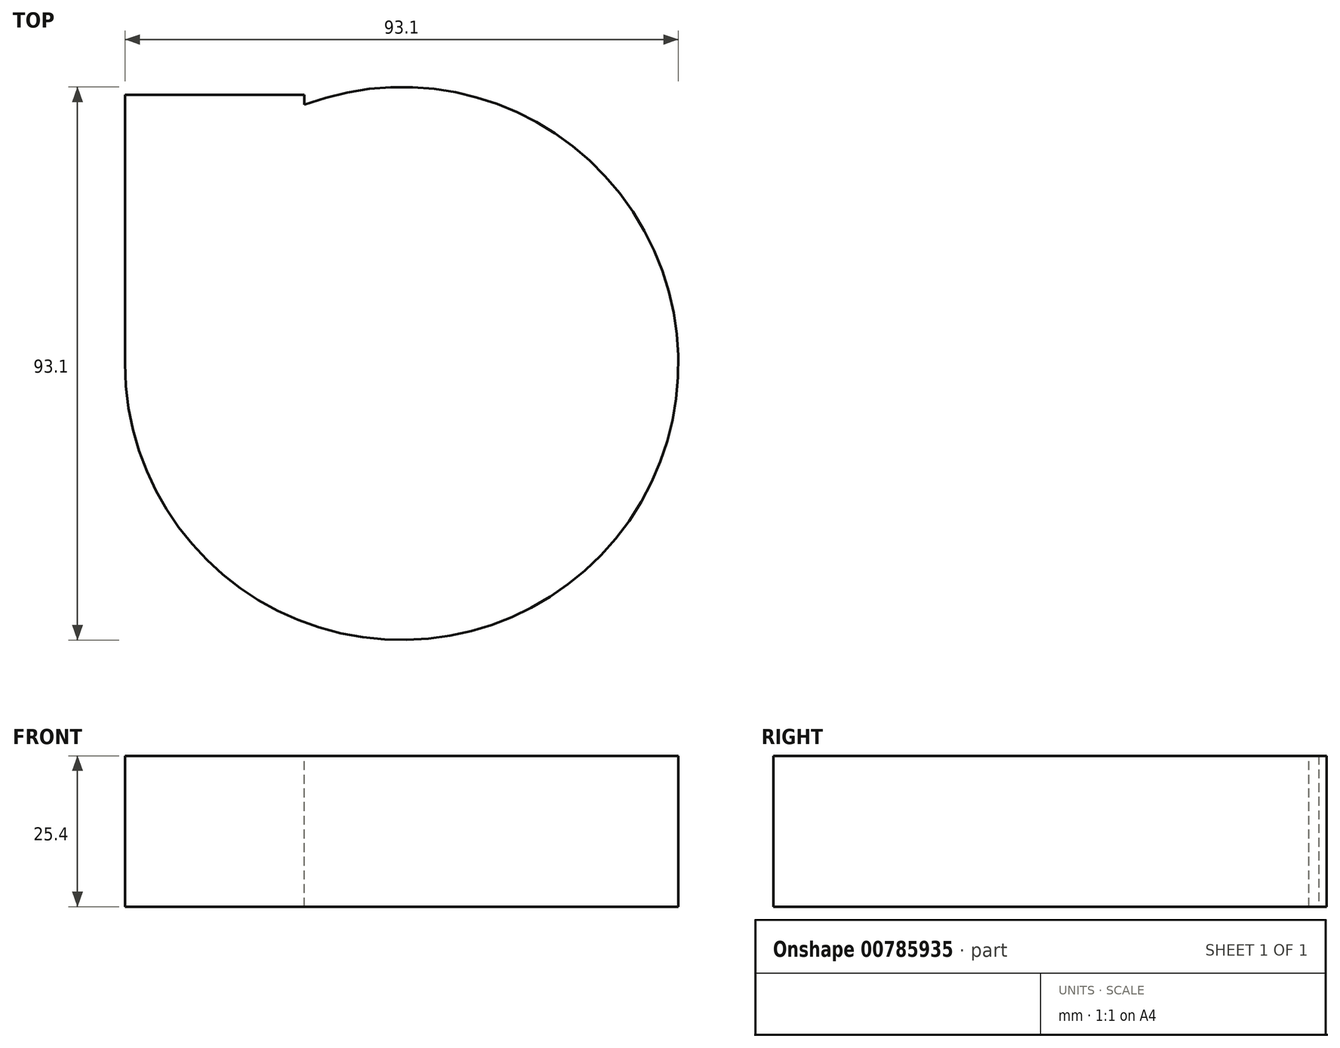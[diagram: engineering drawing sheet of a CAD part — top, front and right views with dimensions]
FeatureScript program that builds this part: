
annotation { "Feature Type Name" : "Feature", "Feature Type Description" : "" }
export const myFeature = defineFeature(function(context is Context, id is Id, definition is map)
    precondition{}
    {
        {
            var Q0;
            Q0=qCreatedBy(makeId("Top.planeOp"),FACE);
            var sketch = newSketch(context, id + "F0", { "sketchPlane" : qUnion([Q0])});
            skLineSegment(sketch, "E0.bottom", {"start": v(0, 0) * mm, "end": v(-30.16, 0) * mm});
            skLineSegment(sketch, "E0.top", {"start": v(0, 45.24) * mm, "end": v(-30.16, 45.24) * mm});
            skLineSegment(sketch, "E0.left", {"start": v(0, 0) * mm, "end": v(0, 45.24) * mm});
            skLineSegment(sketch, "E0.right", {"start": v(-30.16, 0) * mm, "end": v(-30.16, 45.24) * mm});
            skLineSegment(sketch, "E1.bottom", {"start": v(16.4, 0) * mm, "end": v(-7.86, 0) * mm});
            skLineSegment(sketch, "E1.top", {"start": v(16.4, 16.8) * mm, "end": v(-7.86, 16.8) * mm});
            skLineSegment(sketch, "E1.left", {"start": v(16.4, 0) * mm, "end": v(16.4, 16.8) * mm});
            skLineSegment(sketch, "E1.right", {"start": v(-7.86, 0) * mm, "end": v(-7.86, 16.8) * mm});
            skSolve(sketch);
        }
        {
            var Q0;
            Q0 = qSketchRegion(id + "F0", true);
            extrude(context, id + "F1", {"entities" : qUnion([Q0]), "depth" : 25.4 * mm, "offsetDistance" : 25.4 * mm});
        }
        {
            var Q0;
            Q0=makeQuery(id+"F1.opExtrude","SWEPT_FACE",FACE,{"disambiguationData":[OSD([sQuery(id+"F0.wireOp",EDGE,"E0.bottom"),sQuery(id+"F0.wireOp",EDGE,"E1.bottom")])]});
            var Q1;
            Q1=makeQuery(id+"F1.opExtrude","SWEPT_EDGE",EDGE,{"disambiguationData":[OSD([sQuery(id+"F0.wireOp",EDGE,"E1.bottom"),sQuery(id+"F0.wireOp",EDGE,"E1.left")])]});
            revolve(context, id + "F2", {"operationType" : NewBodyOperationType.ADD, "surfaceOperationType" : NewSurfaceOperationType.NEW, "entities" : qUnion([Q0]), "axis" : qUnion([Q1]), "revolveType" : RevolveType.FULL});
        }
    });
